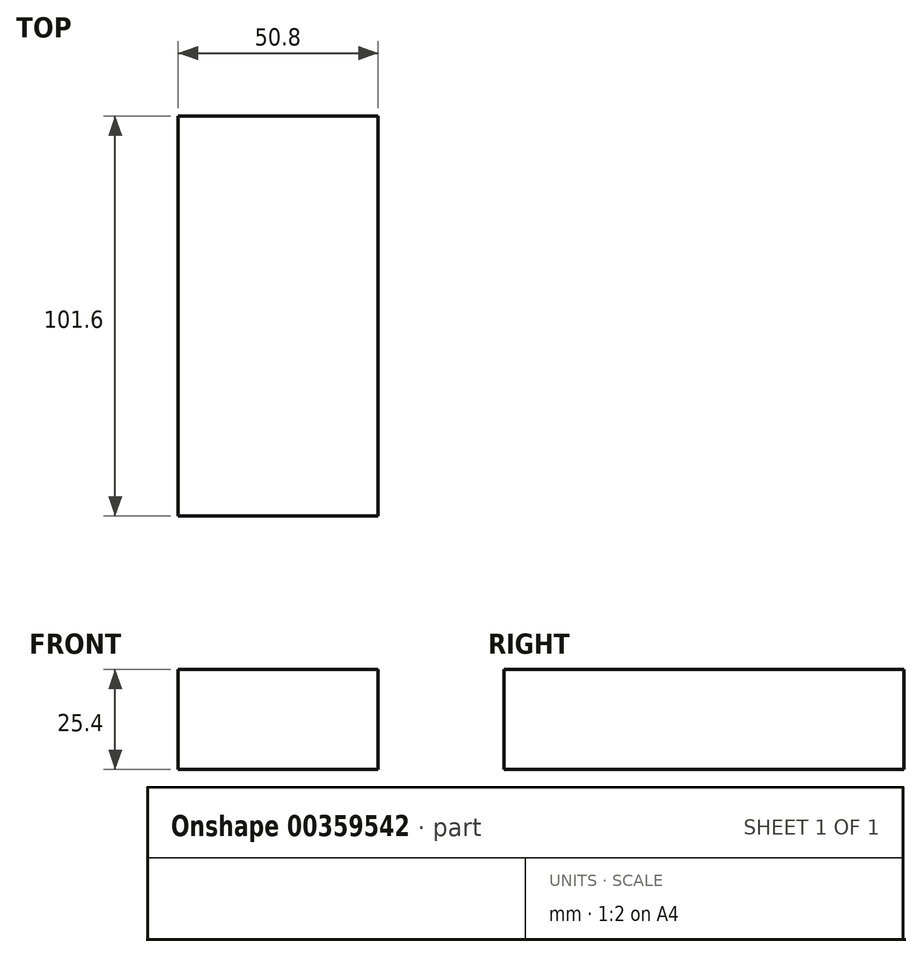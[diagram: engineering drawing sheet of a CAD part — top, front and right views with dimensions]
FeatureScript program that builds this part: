
annotation { "Feature Type Name" : "Feature", "Feature Type Description" : "" }
export const myFeature = defineFeature(function(context is Context, id is Id, definition is map)
    precondition{}
    {
        {
            var Q0;
            Q0=qCreatedBy(makeId("Top.planeOp"),FACE);
            var sketch = newSketch(context, id + "F0", { "sketchPlane" : qUnion([Q0])});
            skLineSegment(sketch, "E0.bottom", {"start": v(0, 0) * mm, "end": v(-50.8, 0) * mm});
            skLineSegment(sketch, "E0.top", {"start": v(0, -101.6) * mm, "end": v(-50.8, -101.6) * mm});
            skLineSegment(sketch, "E0.left", {"start": v(0, 0) * mm, "end": v(0, -101.6) * mm});
            skLineSegment(sketch, "E0.right", {"start": v(-50.8, 0) * mm, "end": v(-50.8, -101.6) * mm});
            skSolve(sketch);
        }
        {
            var Q0;
            Q0 = qSketchRegion(id + "F0", true);
            extrude(context, id + "F1", {"entities" : qUnion([Q0]), "depth" : 25.4 * mm});
        }
    });
